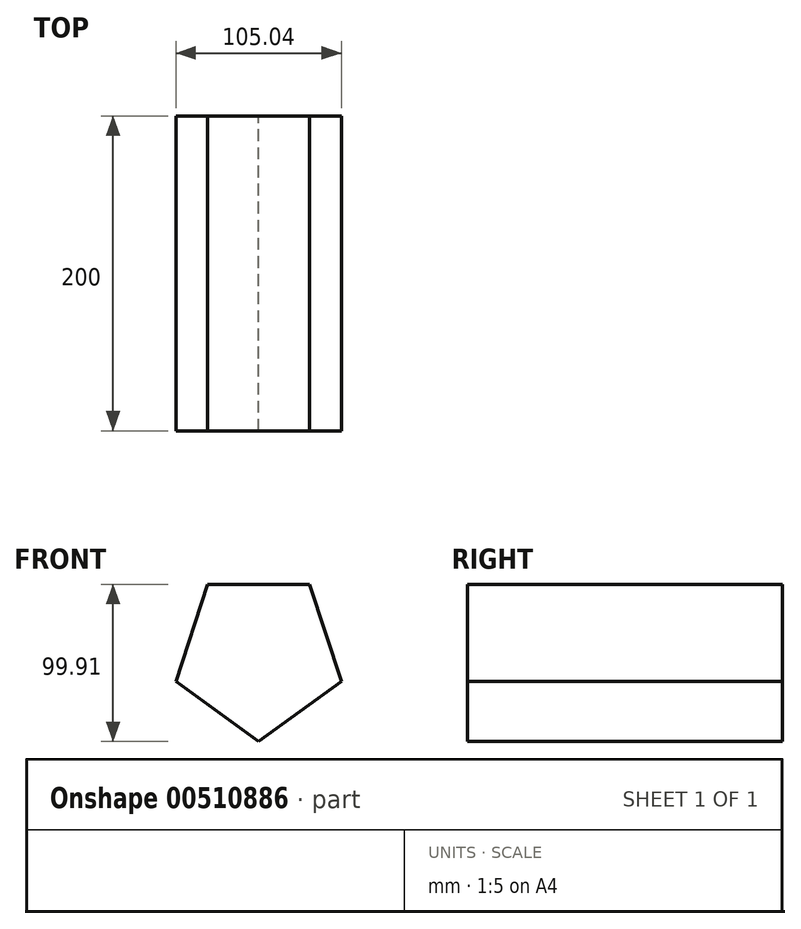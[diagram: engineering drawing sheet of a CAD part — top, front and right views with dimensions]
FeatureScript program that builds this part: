
annotation { "Feature Type Name" : "Feature", "Feature Type Description" : "" }
export const myFeature = defineFeature(function(context is Context, id is Id, definition is map)
    precondition{}
    {
        {
            var Q0;
            Q0=qCreatedBy(makeId("Front.planeOp"),FACE);
            var sketch = newSketch(context, id + "F0", { "sketchPlane" : qUnion([Q0])});
            skCircle(sketch, "E0.cCircle", {"center": v(0, 0) * mm, "radius": 55.23 * mm, "construction": true});
            skLineSegment(sketch, "E0.0", {"start": v(0, -55.23) * mm, "end": v(-52.52, -17.07) * mm});
            skLineSegment(sketch, "E0.1", {"start": v(-52.52, -17.07) * mm, "end": v(-32.46, 44.68) * mm});
            skLineSegment(sketch, "E0.2", {"start": v(-32.46, 44.68) * mm, "end": v(32.46, 44.68) * mm});
            skLineSegment(sketch, "E0.3", {"start": v(32.46, 44.68) * mm, "end": v(52.52, -17.07) * mm});
            skLineSegment(sketch, "E0.4", {"start": v(52.52, -17.07) * mm, "end": v(0, -55.23) * mm});
            skSolve(sketch);
        }
        {
            var Q0;
            Q0=qSketchRegion(id+"F0",true);
            extrude(context, id + "F1", {"entities" : qUnion([Q0]), "depth" : 200 * mm});
        }
    });
